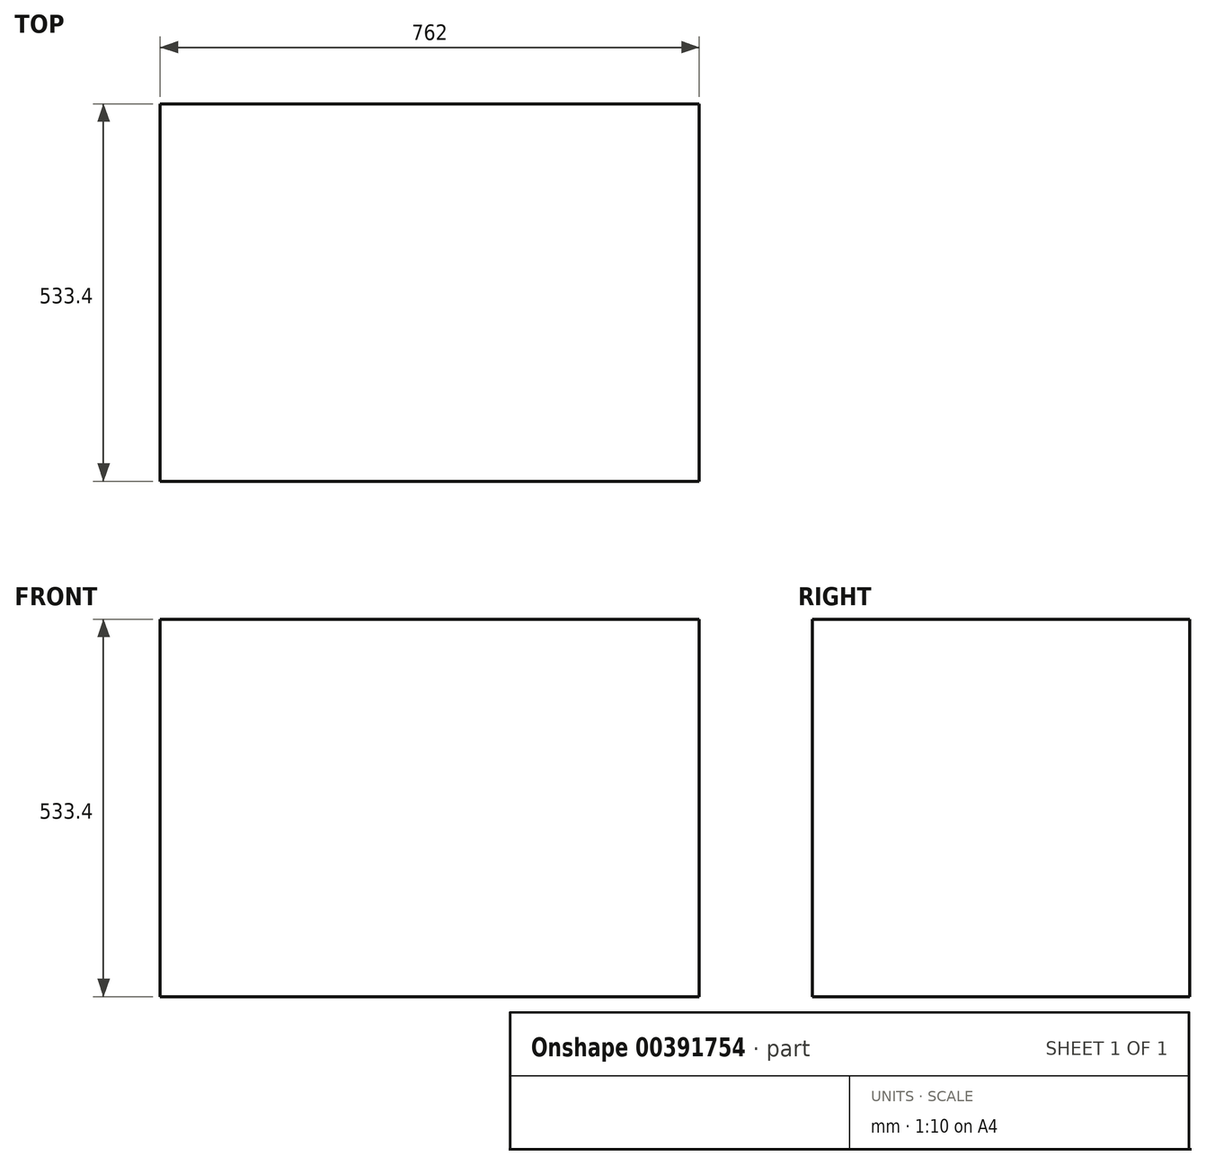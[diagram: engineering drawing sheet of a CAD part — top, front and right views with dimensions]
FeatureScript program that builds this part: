
annotation { "Feature Type Name" : "Feature", "Feature Type Description" : "" }
export const myFeature = defineFeature(function(context is Context, id is Id, definition is map)
    precondition{}
    {
        {
            var Q0;
            Q0=qCreatedBy(makeId("Front.planeOp"),FACE);
            var sketch = newSketch(context, id + "F0", { "sketchPlane" : qUnion([Q0])});
            skLineSegment(sketch, "E0.bottom", {"start": v(381, 266.7) * mm, "end": v(-381, 266.7) * mm});
            skLineSegment(sketch, "E0.top", {"start": v(381, -266.7) * mm, "end": v(-381, -266.7) * mm});
            skLineSegment(sketch, "E0.left", {"start": v(381, 266.7) * mm, "end": v(381, -266.7) * mm});
            skLineSegment(sketch, "E0.right", {"start": v(-381, 266.7) * mm, "end": v(-381, -266.7) * mm});
            skPoint(sketch, "E0.middle", {"position": v(0, 0) * mm});
            skSolve(sketch);
        }
        {
            var Q0;
            Q0 = qSketchRegion(id + "F0", true);
            extrude(context, id + "F1", {"entities" : qUnion([Q0]), "oppositeDirection" : true, "depth" : 533.4 * mm, "offsetDistance" : 25.4 * mm});
        }
    });
